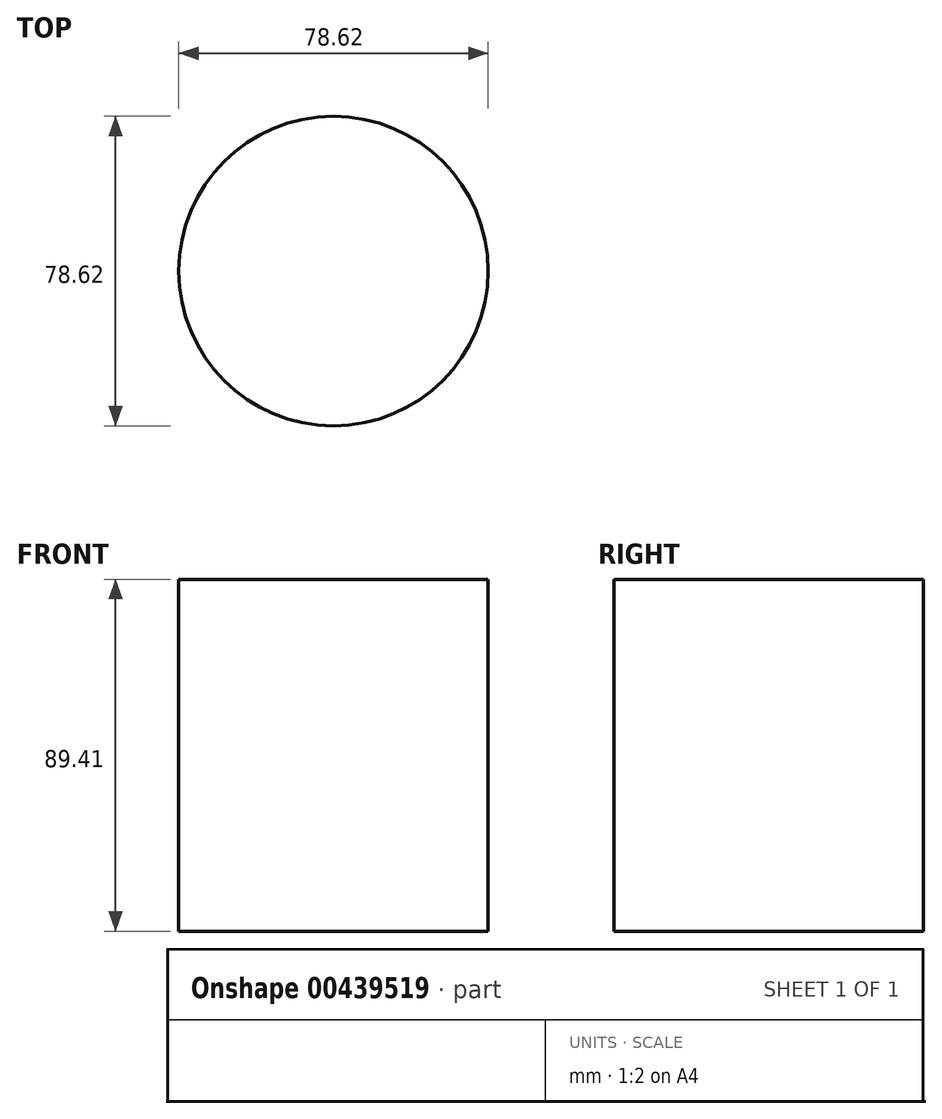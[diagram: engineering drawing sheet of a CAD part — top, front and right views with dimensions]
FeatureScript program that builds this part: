
annotation { "Feature Type Name" : "Feature", "Feature Type Description" : "" }
export const myFeature = defineFeature(function(context is Context, id is Id, definition is map)
    precondition{}
    {
        {
            var Q0;
            Q0=qCreatedBy(makeId("Top.planeOp"),FACE);
            var sketch = newSketch(context, id + "F0", { "sketchPlane" : qUnion([Q0])});
            skCircle(sketch, "E0", {"center": v(0, 0) * mm, "radius": 39.3 * mm});
            skSolve(sketch);
        }
        {
            var Q0;
            Q0=makeQuery(id+"F0.imprint","IMPRINT",FACE,{"disambiguationData":[TD([[makeQuery(id+"F0.imprint","IMPRINT",EDGE,{"derivedFrom":sQuery(id+"F0.wireOp",EDGE,"E0")}),1.0]])]});
            extrude(context, id + "F1", {"entities" : qUnion([Q0]), "depth" : 89.4 * mm});
        }
    });
